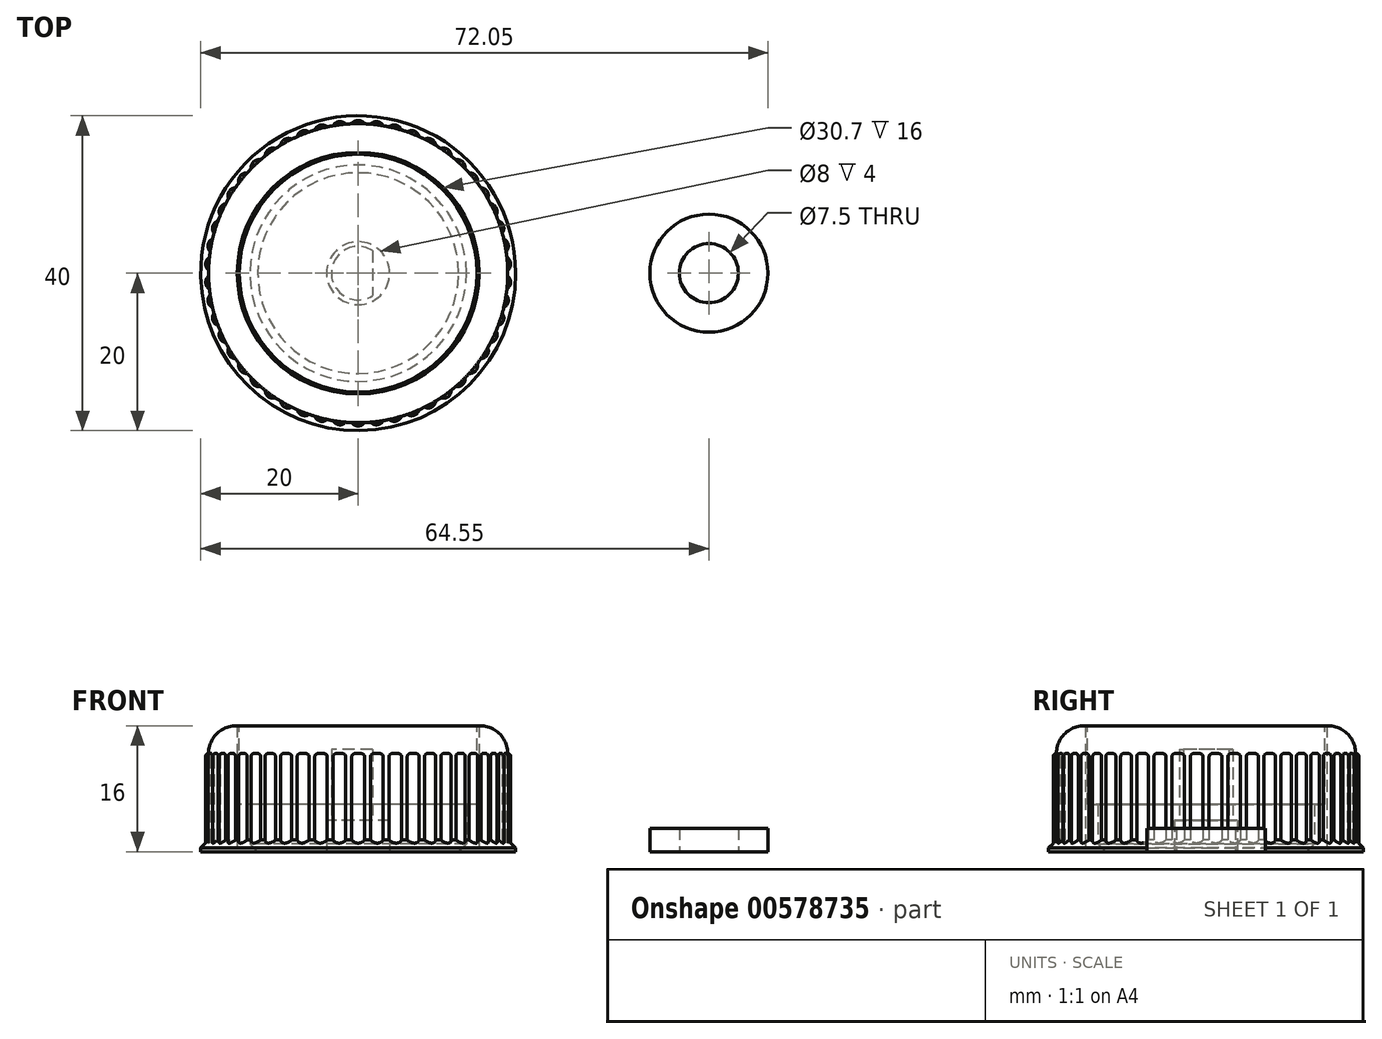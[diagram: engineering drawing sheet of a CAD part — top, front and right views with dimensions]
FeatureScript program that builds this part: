
annotation { "Feature Type Name" : "Feature", "Feature Type Description" : "" }
export const myFeature = defineFeature(function(context is Context, id is Id, definition is map)
    precondition{}
    {
        {
            var Q0;
            Q0=qCreatedBy(makeId("Top.planeOp"),FACE);
            var sketch = newSketch(context, id + "F0", { "sketchPlane" : qUnion([Q0])});
            skCircle(sketch, "E0", {"center": v(0, 0) * mm, "radius": 19 * mm});
            skCircle(sketch, "E1", {"center": v(0, 0) * mm, "radius": 15.35 * mm});
            skCircle(sketch, "E2", {"center": v(0, 0) * mm, "radius": 13.75 * mm});
            skArc(sketch, "E3", {"start": v(1.83, 2.87) * mm, "mid": v(-3.4, 0) * mm, "end": v(1.83, -2.87) * mm});
            skCircle(sketch, "E4", {"center": v(0, 0) * mm, "radius": 4 * mm});
            skLineSegment(sketch, "E5", {"start": v(1.83, 2.87) * mm, "end": v(1.83, -2.87) * mm});
            skCircle(sketch, "E6", {"center": v(0, 0) * mm, "radius": 20 * mm});
            skCircle(sketch, "E7", {"center": v(44.55, 0) * mm, "radius": 3.75 * mm});
            skPoint(sketch, "E7.centerSnap0", {"position": v(-3.4, 0) * mm});
            skCircle(sketch, "E8", {"center": v(44.55, 0) * mm, "radius": 7.5 * mm});
            skSolve(sketch);
        }
        {
            var Q0;
            Q0=makeQuery(id+"F0.imprint","IMPRINT",FACE,{"disambiguationData":[TD([[makeQuery(id+"F0.imprint","IMPRINT",EDGE,{"derivedFrom":sQuery(id+"F0.wireOp",EDGE,"E0")}),1.0]])]});
            var Q1;
            Q1=makeQuery(id+"F0.imprint","IMPRINT",FACE,{"disambiguationData":[TD([[makeQuery(id+"F0.imprint","IMPRINT",EDGE,{"derivedFrom":sQuery(id+"F0.wireOp",EDGE,"E2")}),1.0]])]});
            var Q2;
            Q2=makeQuery(id+"F0.imprint","IMPRINT",FACE,{"disambiguationData":[TD([[makeQuery(id+"F0.imprint","IMPRINT",EDGE,{"derivedFrom":sQuery(id+"F0.wireOp",EDGE,"E3")}),-1.0]])]});
            var Q3;
            Q3=makeQuery(id+"F0.imprint","IMPRINT",FACE,{"disambiguationData":[TD([[makeQuery(id+"F0.imprint","IMPRINT",EDGE,{"derivedFrom":sQuery(id+"F0.wireOp",EDGE,"E1")}),1.0]])]});
            var Q4;
            Q4=makeQuery(id+"F0.imprint","IMPRINT",FACE,{"disambiguationData":[TD([[makeQuery(id+"F0.imprint","IMPRINT",EDGE,{"derivedFrom":sQuery(id+"F0.wireOp",EDGE,"E3")}),1.0]])]});
            extrude(context, id + "F1", {"entities" : qUnion([Q0, Q1, Q2, Q3, Q4]), "depth" : 16 * mm, "offsetDistance" : 25 * mm});
        }
        {
            var Q0;
            Q0=makeQuery(id+"F0.imprint","IMPRINT",FACE,{"disambiguationData":[TD([[makeQuery(id+"F0.imprint","IMPRINT",EDGE,{"derivedFrom":sQuery(id+"F0.wireOp",EDGE,"E1")}),1.0]])]});
            extrude(context, id + "F2", {"entities" : qUnion([Q0]), "operationType" : NewBodyOperationType.REMOVE, "depth" : 22 * mm, "offsetDistance" : 25 * mm});
        }
        {
            var Q0;
            Q0=makeQuery(id+"F0.imprint","IMPRINT",FACE,{"disambiguationData":[TD([[makeQuery(id+"F0.imprint","IMPRINT",EDGE,{"derivedFrom":sQuery(id+"F0.wireOp",EDGE,"E3")}),1.0]])]});
            extrude(context, id + "F3", {"entities" : qUnion([Q0]), "operationType" : NewBodyOperationType.REMOVE, "depth" : 13 * mm, "offsetDistance" : 25 * mm});
        }
        {
            var Q0;
            Q0=makeQuery(id+"F1.opExtrude","CAP_EDGE",EDGE,{"disambiguationData":[OSD([sQuery(id+"F0.wireOp",EDGE,"E0")])],"isStart":false});
            fillet(context, id + "F4", {"entities" : qUnion([Q0]), "radius" : 3.5 * mm, "tangentPropagation" : true, "allowEdgeOverflow" : false});
        }
        {
            var Q0;
            Q0=makeQuery(id+"F0.imprint","IMPRINT",FACE,{"disambiguationData":[TD([[makeQuery(id+"F0.imprint","IMPRINT",EDGE,{"derivedFrom":sQuery(id+"F0.wireOp",EDGE,"E0")}),1.0]])]});
            var sketch = newSketch(context, id + "F5", { "sketchPlane" : qUnion([Q0])});
            skArc(sketch, "E9", {"start": v(-0.82, -18.97) * mm, "mid": v(0, -19.41) * mm, "end": v(0.82, -18.97) * mm});
            skSolve(sketch);
        }
        {
            var Q0;
            {var subQ0=sQuery(id+"F5.wireOp",EDGE,"E9");var subQ1=makeQuery(id+"F0.imprint","IMPRINT",EDGE,{"derivedFrom":sQuery(id+"F0.wireOp",EDGE,"E0")});var subQ2=makeQuery(id+"F5.imprint","INTERSECT",VERTEX,{"disambiguationData":[OD(0.0)],"derivedFrom":[subQ1,subQ0]});Q0=makeQuery(id+"F5.imprint","IMPRINT",FACE,{"disambiguationData":[TD([[makeQuery(id+"F5.imprint","IMPRINT",EDGE,{"disambiguationData":[TD([[subQ2,-1.0]])],"derivedFrom":subQ0}),1.0]])]});}
            extrude(context, id + "F6", {"entities" : qUnion([Q0]), "depth" : 12.5 * mm, "offsetDistance" : 25 * mm});
        }
        {
            var Q0;
            Q0=makeQuery(id+"F6.opExtrude","CAP_EDGE",EDGE,{"disambiguationData":[OSD([sQuery(id+"F5.wireOp",EDGE,"E9")])],"isStart":false});
            fillet(context, id + "F7", {"entities" : qUnion([Q0]), "radius" : 0.4 * mm, "tangentPropagation" : true, "allowEdgeOverflow" : false});
        }
        {
            var Q0;
            Q0=makeQuery(id+"F6.opExtrude","SWEPT_BODY",BODY,{"disambiguationData":[OSD([sQuery(id+"F0.wireOp",EDGE,"E0"),sQuery(id+"F5.wireOp",EDGE,"E9")])]});
            var Q1;
            Q1=makeQuery(id+"F1.opExtrude","SWEPT_FACE",FACE,{"disambiguationData":[OSD([sQuery(id+"F0.wireOp",EDGE,"E0")])]});
            circularPattern(context, id + "F8", {"operationType" : NewBodyOperationType.ADD, "entities" : qUnion([Q0]), "axis" : qUnion([Q1]), "angle" : 360 * degree, "instanceCount" : 50, "equalSpace" : true});
        }
        {
            var Q0;
            Q0=makeQuery(id+"F0.imprint","IMPRINT",FACE,{"disambiguationData":[TD([[makeQuery(id+"F0.imprint","IMPRINT",EDGE,{"derivedFrom":sQuery(id+"F0.wireOp",EDGE,"E0")}),-1.0]])]});
            extrude(context, id + "F9", {"entities" : qUnion([Q0]), "operationType" : NewBodyOperationType.ADD, "depth" : 2 * mm, "offsetDistance" : 25 * mm});
        }
        {
            var Q0;
            Q0=makeQuery(id+"F9.opExtrude","CAP_EDGE",EDGE,{"disambiguationData":[OSD([sQuery(id+"F0.wireOp",EDGE,"E6")])],"isStart":false});
            chamfer(context, id + "F10", {"entities" : qUnion([Q0]), "width" : 1.5 * mm, "tangentPropagation" : true});
        }
        {
            var Q0;
            Q0=makeQuery(id+"F2.boolean.opBoolean","COPY",EDGE,{"derivedFrom":makeQuery(id+"F2.opExtrude","CAP_EDGE",EDGE,{"disambiguationData":[OSD([sQuery(id+"F0.wireOp",EDGE,"E2")])],"isStart":true})});
            var Q1;
            Q1=makeQuery(id+"F2.boolean.opBoolean","COPY",EDGE,{"derivedFrom":makeQuery(id+"F2.opExtrude","CAP_EDGE",EDGE,{"disambiguationData":[OSD([sQuery(id+"F0.wireOp",EDGE,"E1")])],"isStart":true})});
            chamfer(context, id + "F11", {"entities" : qUnion([Q0, Q1]), "width" : 1 * mm, "tangentPropagation" : true});
        }
        {
            var Q0;
            Q0=makeQuery(id+"F2.boolean.opBoolean","SPLIT",FACE,{"disambiguationData":[TD([makeQuery(id+"F2.opExtrude","SWEPT_FACE",FACE,{"disambiguationData":[OSD([sQuery(id+"F0.wireOp",EDGE,"E2")])]})])],"derivedFrom":makeQuery(id+"F1.opExtrude","CAP_FACE",FACE,{"disambiguationData":[OSD([sQuery(id+"F0.wireOp",EDGE,"E0")])],"isStart":false})});
            var sketch = newSketch(context, id + "F12", { "sketchPlane" : qUnion([Q0])});
            skCircle(sketch, "E10", {"center": v(0, 0) * mm, "radius": 15.1 * mm});
            skSolve(sketch);
        }
        {
            var Q0;
            Q0=makeQuery(id+"F12.imprint","IMPRINT",FACE,{"disambiguationData":[TD([[makeQuery(id+"F12.imprint","IMPRINT",EDGE,{"derivedFrom":sQuery(id+"F12.wireOp",EDGE,"E10")}),1.0]])]});
            extrude(context, id + "F13", {"entities" : qUnion([Q0]), "operationType" : NewBodyOperationType.ADD, "oppositeDirection" : true, "depth" : 10 * mm, "offsetDistance" : 25 * mm});
        }
        {
            var Q0;
            Q0=makeQuery(id+"F0.imprint","IMPRINT",FACE,{"disambiguationData":[TD([[makeQuery(id+"F0.imprint","IMPRINT",EDGE,{"derivedFrom":sQuery(id+"F0.wireOp",EDGE,"E3")}),-1.0]])]});
            extrude(context, id + "F14", {"entities" : qUnion([Q0]), "operationType" : NewBodyOperationType.REMOVE, "depth" : 4 * mm, "offsetDistance" : 25 * mm});
        }
        {
            var Q0;
            Q0=makeQuery(id+"F0.imprint","IMPRINT",FACE,{"disambiguationData":[TD([[makeQuery(id+"F0.imprint","IMPRINT",EDGE,{"derivedFrom":sQuery(id+"F0.wireOp",EDGE,"E7")}),-1.0]])]});
            extrude(context, id + "F15", {"entities" : qUnion([Q0]), "depth" : 3 * mm, "offsetDistance" : 25 * mm});
        }
    });
